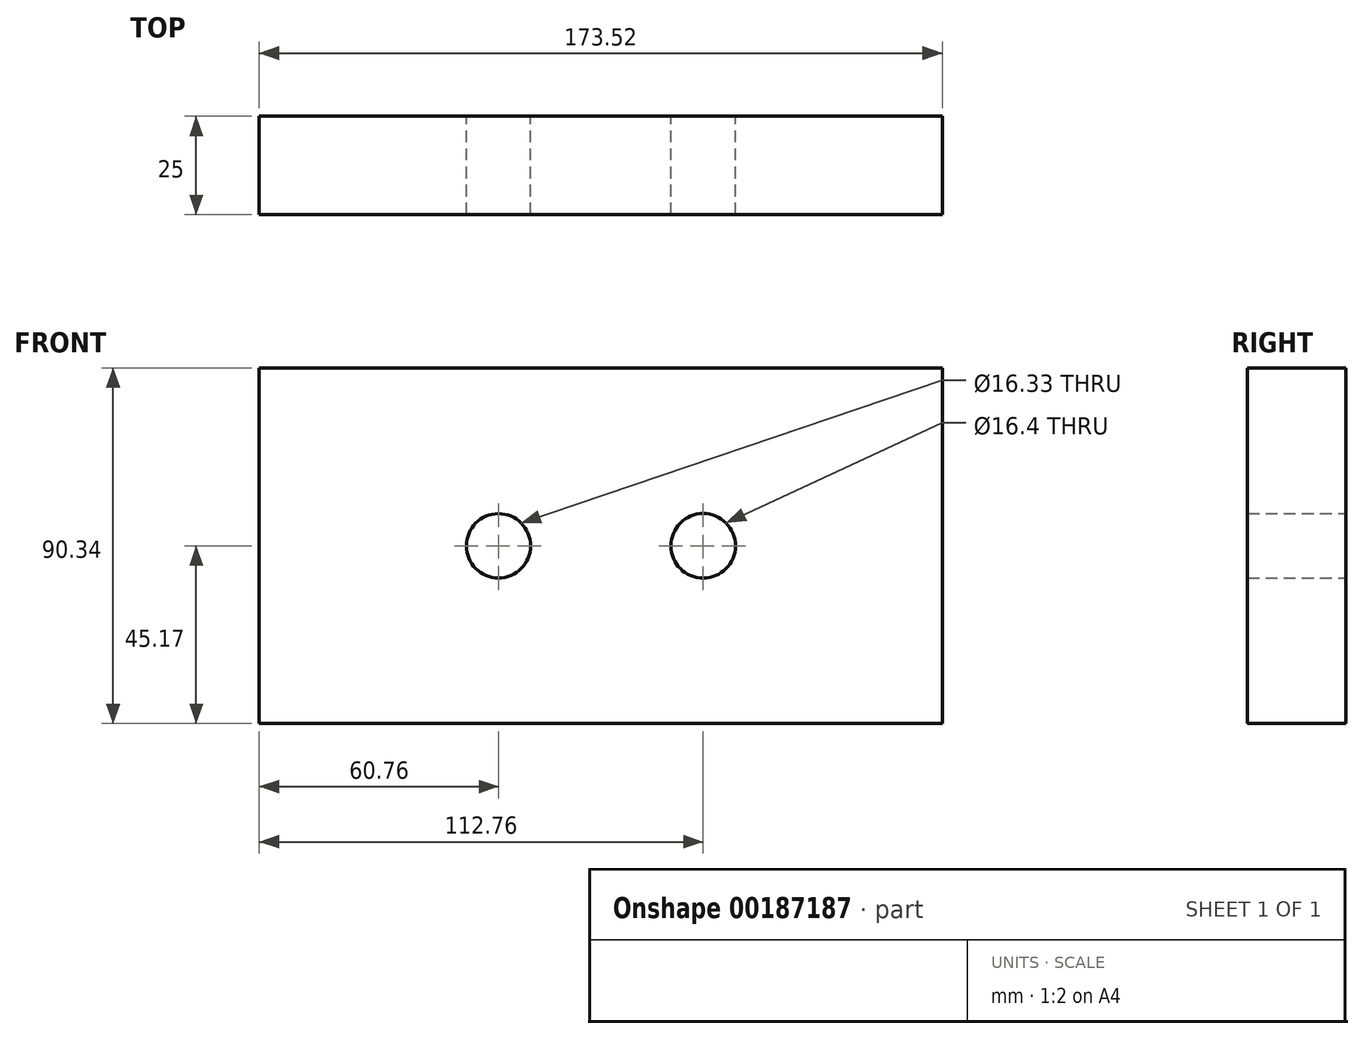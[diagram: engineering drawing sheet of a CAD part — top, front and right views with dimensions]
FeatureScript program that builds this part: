
annotation { "Feature Type Name" : "Feature", "Feature Type Description" : "" }
export const myFeature = defineFeature(function(context is Context, id is Id, definition is map)
    precondition{}
    {
        {
            var Q0;
            Q0=qCreatedBy(makeId("Front.planeOp"),FACE);
            var sketch = newSketch(context, id + "F0", { "sketchPlane" : qUnion([Q0])});
            skLineSegment(sketch, "E0.bottom", {"start": v(-86.76, 45.17) * mm, "end": v(86.76, 45.17) * mm});
            skLineSegment(sketch, "E0.top", {"start": v(-86.76, -45.17) * mm, "end": v(86.76, -45.17) * mm});
            skLineSegment(sketch, "E0.left", {"start": v(-86.76, 45.17) * mm, "end": v(-86.76, -45.17) * mm});
            skLineSegment(sketch, "E0.right", {"start": v(86.76, 45.17) * mm, "end": v(86.76, -45.17) * mm});
            skPoint(sketch, "E0.middle", {"position": v(0, 0) * mm});
            skCircle(sketch, "E1", {"center": v(-26, 0) * mm, "radius": 8.16 * mm});
            skCircle(sketch, "E2", {"center": v(26, 0) * mm, "radius": 8.2 * mm});
            skSolve(sketch);
        }
        {
            var Q0;
            Q0=makeQuery(id+"F0.imprint","IMPRINT",FACE,{"disambiguationData":[TD([[makeQuery(id+"F0.imprint","IMPRINT",EDGE,{"derivedFrom":sQuery(id+"F0.wireOp",EDGE,"E0.bottom")}),-1.0]])]});
            extrude(context, id + "F1", {"entities" : qUnion([Q0]), "depth" : 25 * mm});
        }
    });
